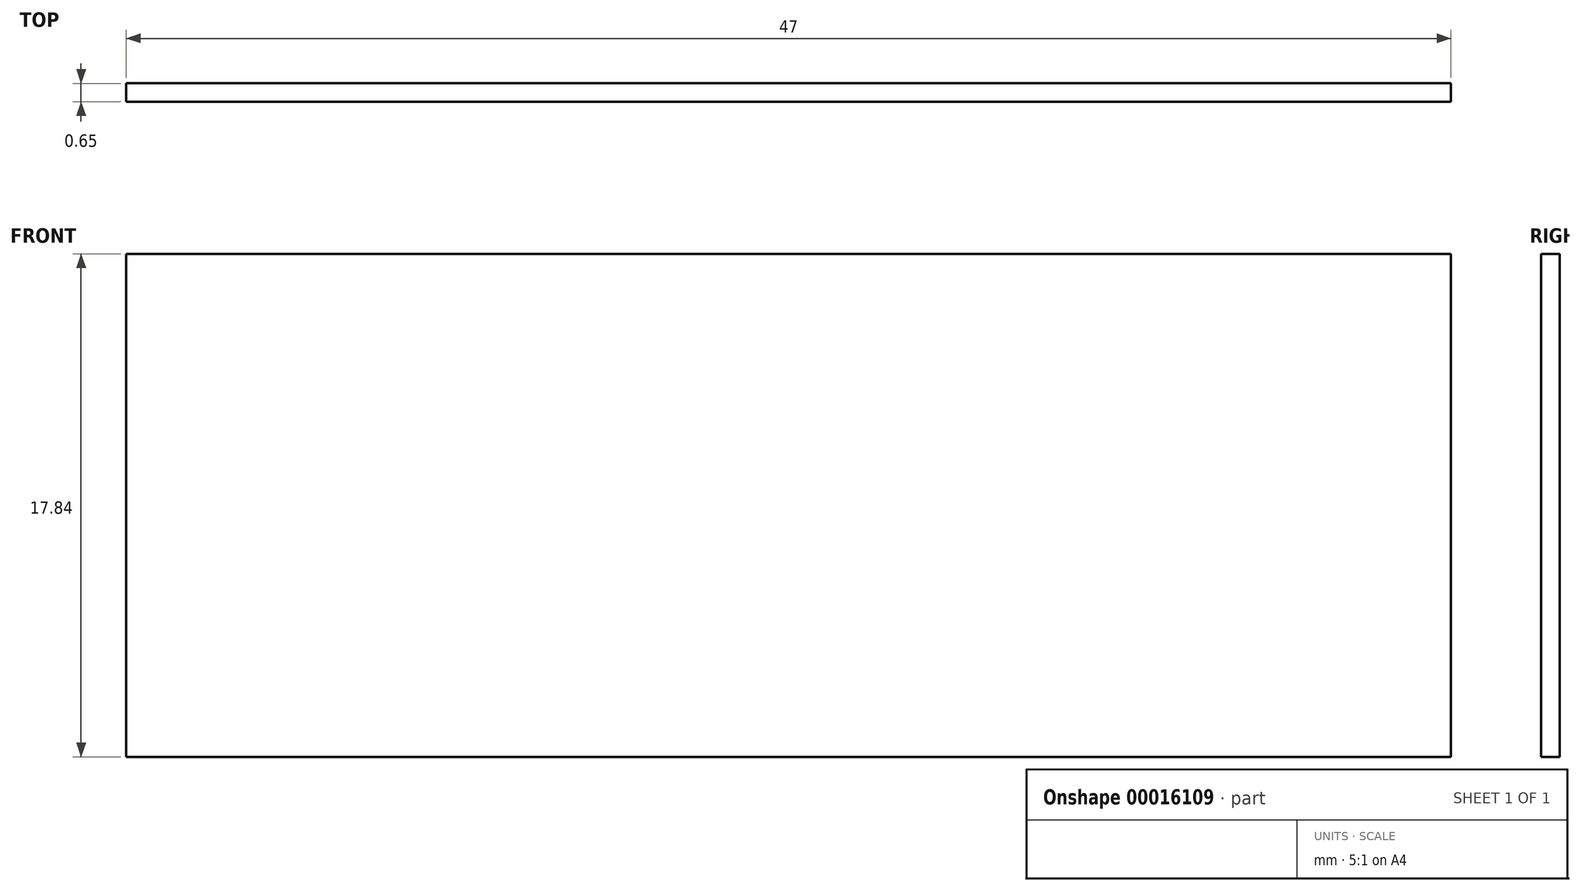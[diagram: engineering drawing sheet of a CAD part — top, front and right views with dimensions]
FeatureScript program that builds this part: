
annotation { "Feature Type Name" : "Feature", "Feature Type Description" : "" }
export const myFeature = defineFeature(function(context is Context, id is Id, definition is map)
    precondition{}
    {
        {
            var Q0;
            Q0=qCreatedBy(makeId("Front.planeOp"),FACE);
            var sketch = newSketch(context, id + "F0", { "sketchPlane" : qUnion([Q0])});
            skLineSegment(sketch, "E0.rect.bottom", {"start": v(23.5, -8.92) * mm, "end": v(-23.5, -8.92) * mm});
            skLineSegment(sketch, "E0.rect.top", {"start": v(23.5, 8.92) * mm, "end": v(-23.5, 8.92) * mm});
            skLineSegment(sketch, "E0.rect.left", {"start": v(23.5, -8.92) * mm, "end": v(23.5, 8.92) * mm});
            skLineSegment(sketch, "E0.rect.right", {"start": v(-23.5, -8.92) * mm, "end": v(-23.5, 8.92) * mm});
            skPoint(sketch, "E0.rect.middle", {"position": v(0, 0) * mm});
            skSolve(sketch);
        }
        {
            var Q0;
            Q0=makeQuery(id+"F0.imprint","IMPRINT",FACE,{"disambiguationData":[TD([[makeQuery(id+"F0.imprint","IMPRINT",EDGE,{"derivedFrom":sQuery(id+"F0.wireOp",EDGE,"E0.rect.bottom")}),-1.0]])]});
            extrude(context, id + "F1", {"entities" : qUnion([Q0]), "oppositeDirection" : true, "depth" : 0.65 * mm});
        }
    });
